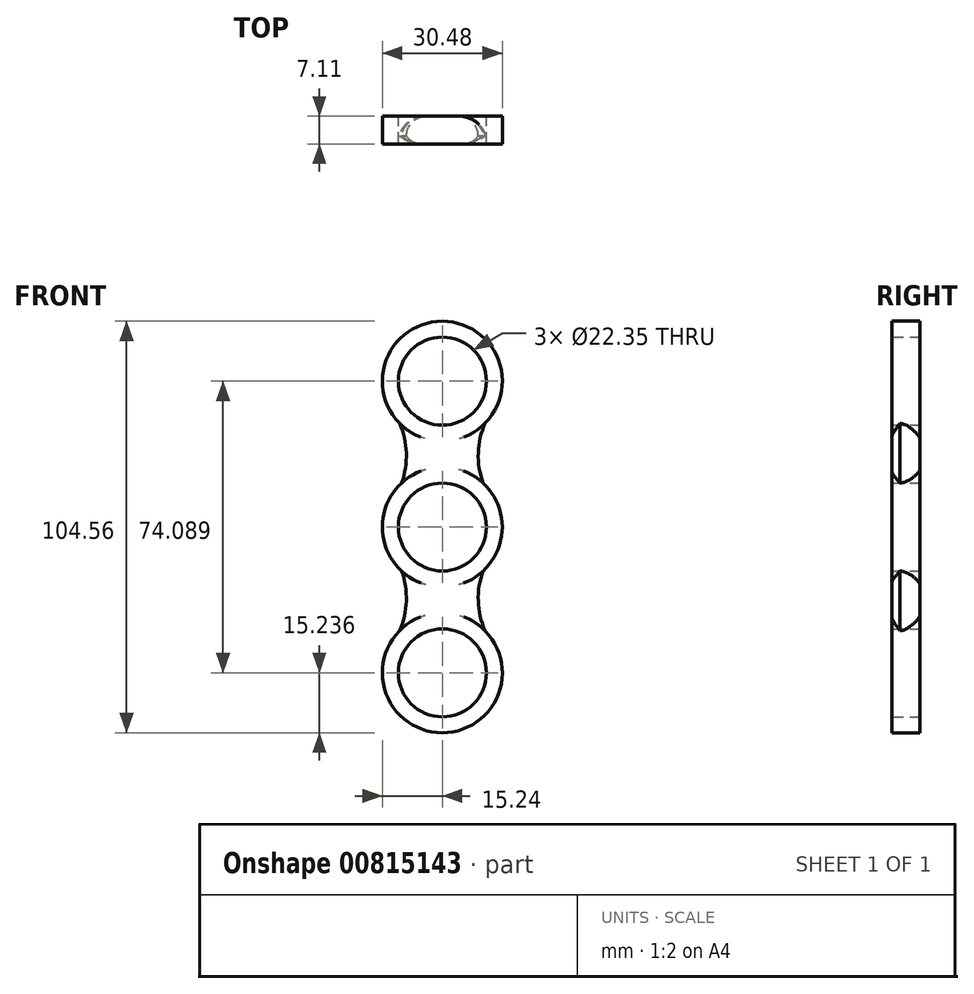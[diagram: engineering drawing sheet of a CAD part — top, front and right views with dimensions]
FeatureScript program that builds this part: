
annotation { "Feature Type Name" : "Feature", "Feature Type Description" : "" }
export const myFeature = defineFeature(function(context is Context, id is Id, definition is map)
    precondition{}
    {
        {
            var Q0;
            Q0=qCreatedBy(makeId("Front.planeOp"),FACE);
            var sketch = newSketch(context, id + "F0", { "sketchPlane" : qUnion([Q0])});
            skCircle(sketch, "E0", {"center": v(0, 0) * mm, "radius": 11.18 * mm});
            skCircle(sketch, "E1", {"center": v(0, 0) * mm, "radius": 15.24 * mm});
            skCircle(sketch, "E2", {"center": v(0, 37.04) * mm, "radius": 15.24 * mm});
            skCircle(sketch, "E3", {"center": v(0, 37.04) * mm, "radius": 11.18 * mm});
            skCircle(sketch, "E4.MirrorC", {"center": v(0, -37.04) * mm, "radius": 11.18 * mm});
            skCircle(sketch, "E5.MirrorC", {"center": v(0, -37.04) * mm, "radius": 15.24 * mm});
            skArc(sketch, "E6", {"start": v(-10.36, 11.18) * mm, "mid": v(-9.14, 18.82) * mm, "end": v(-10.87, 26.37) * mm});
            skArc(sketch, "E7.MirrorCS", {"start": v(10.36, 11.18) * mm, "mid": v(9.14, 18.82) * mm, "end": v(10.87, 26.37) * mm});
            skArc(sketch, "E8.MirrorCS", {"start": v(-10.36, -11.18) * mm, "mid": v(-9.14, -18.82) * mm, "end": v(-10.87, -26.37) * mm});
            skArc(sketch, "E9.MirrorCS", {"start": v(10.36, -11.18) * mm, "mid": v(9.14, -18.82) * mm, "end": v(10.87, -26.37) * mm});
            skSolve(sketch);
        }
        {
            var Q0;
            Q0 = qSketchRegion(id + "F0", true);
            extrude(context, id + "F1", {"entities" : qUnion([Q0]), "depth" : 7.11 * mm, "offsetDistance" : 25.4 * mm});
        }
        {
            var Q0;
            Q0=makeQuery(id+"F1.opExtrude","CAP_EDGE",EDGE,{"disambiguationData":[OSD([sQuery(id+"F0.wireOp",EDGE,"E9.MirrorCS")])],"isStart":true});
            var Q1;
            Q1=makeQuery(id+"F1.opExtrude","CAP_EDGE",EDGE,{"disambiguationData":[OSD([sQuery(id+"F0.wireOp",EDGE,"E8.MirrorCS")])],"isStart":true});
            fillet(context, id + "F2", {"entities" : qUnion([Q0, Q1]), "radius" : 5.08 * mm, "tangentPropagation" : true, "allowEdgeOverflow" : false});
        }
        {
            var Q0;
            Q0=makeQuery(id+"F1.opExtrude","CAP_EDGE",EDGE,{"disambiguationData":[OSD([sQuery(id+"F0.wireOp",EDGE,"E7.MirrorCS")])],"isStart":true});
            var Q1;
            Q1=makeQuery(id+"F1.opExtrude","CAP_EDGE",EDGE,{"disambiguationData":[OSD([sQuery(id+"F0.wireOp",EDGE,"E6")])],"isStart":true});
            fillet(context, id + "F3", {"entities" : qUnion([Q0, Q1]), "radius" : 5.08 * mm, "tangentPropagation" : true, "allowEdgeOverflow" : false});
        }
        {
            var Q0;
            Q0=makeQuery(id+"F1.opExtrude","CAP_EDGE",EDGE,{"disambiguationData":[OSD([sQuery(id+"F0.wireOp",EDGE,"E9.MirrorCS")])],"isStart":false});
            var Q1;
            Q1=makeQuery(id+"F1.opExtrude","CAP_EDGE",EDGE,{"disambiguationData":[OSD([sQuery(id+"F0.wireOp",EDGE,"E8.MirrorCS")])],"isStart":false});
            var Q2;
            Q2=makeQuery(id+"F1.opExtrude","CAP_EDGE",EDGE,{"disambiguationData":[OSD([sQuery(id+"F0.wireOp",EDGE,"E6")])],"isStart":false});
            var Q3;
            Q3=makeQuery(id+"F1.opExtrude","CAP_EDGE",EDGE,{"disambiguationData":[OSD([sQuery(id+"F0.wireOp",EDGE,"E7.MirrorCS")])],"isStart":false});
            fillet(context, id + "F4", {"entities" : qUnion([Q0, Q1, Q2, Q3]), "radius" : 5.08 * mm, "tangentPropagation" : true, "allowEdgeOverflow" : false});
        }
    });
